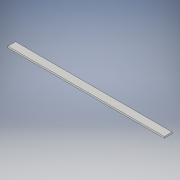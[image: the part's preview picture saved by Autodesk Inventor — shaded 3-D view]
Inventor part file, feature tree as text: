
AUTODESK INVENTOR PART (.ipt)
format: ipt  version: 2017 (Build 210142000, 142)  size: 92,160 bytes
history: native  units: in
note: dims shown in document units (in); Inventor stores cm internally (conversion verified against a paired STEP export)
features: extrude x1, sketch x1
ambient origin geometry x8: Origin, YZ Plane, XZ Plane, XY Plane, X Axis, Y Axis, Z Axis, Center Point
bodies: Solid1 (feature_tree)
feature tree (2):
  extrude  "Extrusion1"  Depth=1.0in
  sketch  "Sketch1"  dims[d0=100.0in d1=1.0in d2=5.0in d3=0.0in]
